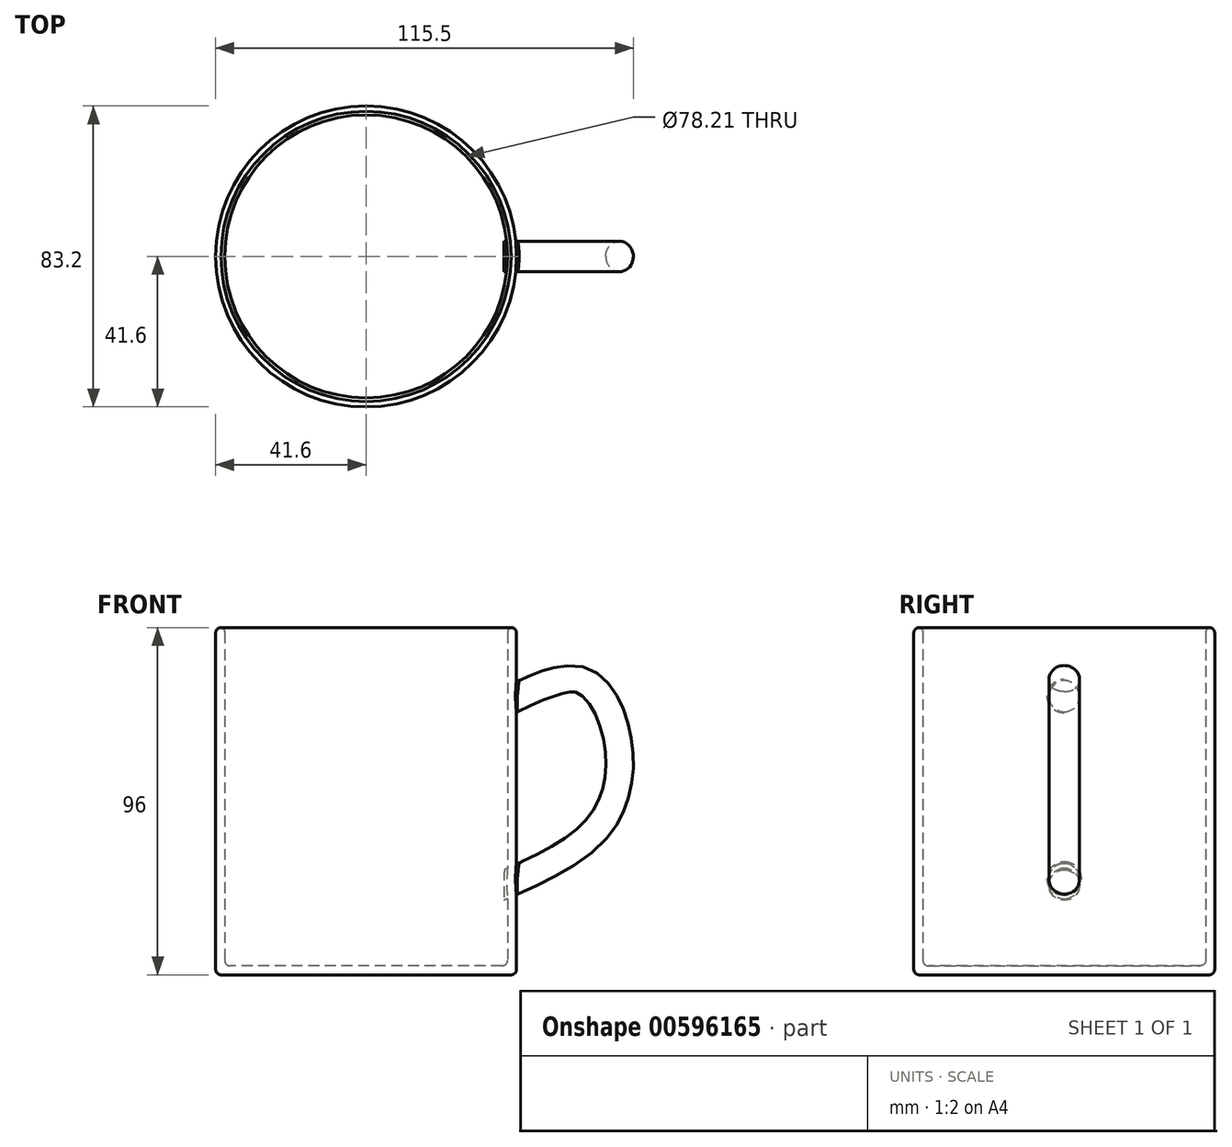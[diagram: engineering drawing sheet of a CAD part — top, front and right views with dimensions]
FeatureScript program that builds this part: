
annotation { "Feature Type Name" : "Feature", "Feature Type Description" : "" }
export const myFeature = defineFeature(function(context is Context, id is Id, definition is map)
    precondition{}
    {
        {
            var Q0;
            Q0=qCreatedBy(makeId("Top.planeOp"),FACE);
            var sketch = newSketch(context, id + "F0", { "sketchPlane" : qUnion([Q0])});
            skCircle(sketch, "E0", {"center": v(0, 0) * mm, "radius": 41.6 * mm});
            skSolve(sketch);
        }
        {
            var Q0;
            Q0=makeQuery(id+"F0.imprint","IMPRINT",FACE,{"disambiguationData":[TD([[makeQuery(id+"F0.imprint","IMPRINT",EDGE,{"derivedFrom":sQuery(id+"F0.wireOp",EDGE,"E0")}),1.0]])]});
            extrude(context, id + "F1", {"entities" : qUnion([Q0]), "depth" : 96 * mm, "offsetDistance" : 25 * mm});
        }
        {
            var Q0;
            Q0=makeQuery(id+"F1.opExtrude","CAP_FACE",FACE,{"disambiguationData":[OSD([sQuery(id+"F0.wireOp",EDGE,"E0")])],"isStart":false});
            shell(context, id + "F2", {"entities" : qUnion([Q0]), "thickness" : 2.5 * mm});
        }
        {
            var Q0;
            Q0=qCreatedBy(makeId("Front.planeOp"),FACE);
            var sketch = newSketch(context, id + "F3", { "sketchPlane" : qUnion([Q0])});
            skFitSpline(sketch, "E1", {"points": [v(39.43, 77.04) * mm, v(60.55, 82) * mm, v(70.77, 63.84) * mm, v(65.16, 40.42) * mm, v(38.1, 23.6) * mm], "startDerivative": vector(98.42, 46.22) * mm, "endDerivative": vector(-111.02, -49.52) * mm});
            skSolve(sketch);
        }
        {
            var Q0;
            Q0=qCreatedBy(makeId("Right.planeOp"),FACE);
            cPlane(context, id + "F4", {"entities" : qUnion([Q0]), "cplaneType" : CPlaneType.OFFSET, "offset" : 41.5 * mm, "width" : 150 * mm, "height" : 150 * mm});
        }
        {
            var Q0;
            Q0=qCreatedBy(id+"F4.planeOp",FACE);
            var sketch = newSketch(context, id + "F5", { "sketchPlane" : qUnion([Q0])});
            skCircle(sketch, "E2", {"center": v(0, 76.8) * mm, "radius": 4.23 * mm});
            skSolve(sketch);
        }
        {
            var Q0;
            Q0 = qSketchRegion(id + "F5", true);
            var Q1;
            Q1 = qConstructionFilter(qBodyType(qCreatedBy(id + "F3" ,EDGE), BodyType.WIRE), ConstructionObject.NO);
            sweep(context, id + "F6", {"operationType" : NewBodyOperationType.ADD, "profiles" : qUnion([Q0]), "path" : qUnion([Q1])});
        }
        {
            var Q0;
            Q0=makeQuery(id+"F1.opExtrude","CAP_EDGE",EDGE,{"disambiguationData":[OSD([sQuery(id+"F0.wireOp",EDGE,"E0")])],"isStart":false});
            fillet(context, id + "F7", {"entities" : qUnion([Q0]), "radius" : 1.5 * mm, "tangentPropagation" : true, "allowEdgeOverflow" : false});
        }
        {
            var Q0;
            {var subQ0=sQuery(id+"F0.wireOp",EDGE,"E0");Q0=makeQuery(id+"F2.opShell","OFFSET_EDGE",EDGE,{"disambiguationData":[OSD([subQ0]),TDD([makeQuery(id+"F1.opExtrude","CAP_EDGE",EDGE,{"disambiguationData":[OSD([subQ0])],"isStart":false})])]});}
            fillet(context, id + "F8", {"entities" : qUnion([Q0]), "radius" : 1.5 * mm, "tangentPropagation" : true, "allowEdgeOverflow" : false});
        }
        {
            var Q0;
            {var subQ0=sQuery(id+"F0.wireOp",EDGE,"E0");Q0=makeQuery(id+"F2.opShell","OFFSET_EDGE",EDGE,{"disambiguationData":[OSD([subQ0]),TDD([makeQuery(id+"F1.opExtrude","CAP_EDGE",EDGE,{"disambiguationData":[OSD([subQ0])],"isStart":true})])]});}
            fillet(context, id + "F9", {"entities" : qUnion([Q0]), "radius" : 1.5 * mm, "tangentPropagation" : true, "allowEdgeOverflow" : false});
        }
        {
            var Q0;
            Q0=makeQuery(id+"F1.opExtrude","CAP_EDGE",EDGE,{"disambiguationData":[OSD([sQuery(id+"F0.wireOp",EDGE,"E0")])],"isStart":true});
            fillet(context, id + "F10", {"entities" : qUnion([Q0]), "radius" : 1.5 * mm, "tangentPropagation" : true, "allowEdgeOverflow" : false});
        }
        {
            var Q0;
            Q0=makeQuery(id+"F6.boolean.opBoolean","INTERSECT",EDGE,{"disambiguationData":[OD(1.0)],"derivedFrom":[makeQuery(id+"F1.opExtrude","SWEPT_FACE",FACE,{"disambiguationData":[OSD([sQuery(id+"F0.wireOp",EDGE,"E0")])]}),makeQuery(id+"F6.opSweep","SWEPT_FACE",FACE,{"disambiguationData":[OSD([sQuery(id+"F3.wireOp",EDGE,"E1"),sQuery(id+"F5.wireOp",EDGE,"E2")])]})]});
            fillet(context, id + "F11", {"entities" : qUnion([Q0]), "radius" : 0.5 * mm, "tangentPropagation" : true, "allowEdgeOverflow" : false});
        }
        {
            var Q0;
            Q0=makeQuery(id+"F6.boolean.opBoolean","INTERSECT",EDGE,{"disambiguationData":[OD(0.0)],"derivedFrom":[makeQuery(id+"F1.opExtrude","SWEPT_FACE",FACE,{"disambiguationData":[OSD([sQuery(id+"F0.wireOp",EDGE,"E0")])]}),makeQuery(id+"F6.opSweep","SWEPT_FACE",FACE,{"disambiguationData":[OSD([sQuery(id+"F3.wireOp",EDGE,"E1"),sQuery(id+"F5.wireOp",EDGE,"E2")])]})]});
            fillet(context, id + "F12", {"entities" : qUnion([Q0]), "radius" : 0.5 * mm, "tangentPropagation" : true, "allowEdgeOverflow" : false});
        }
    });
